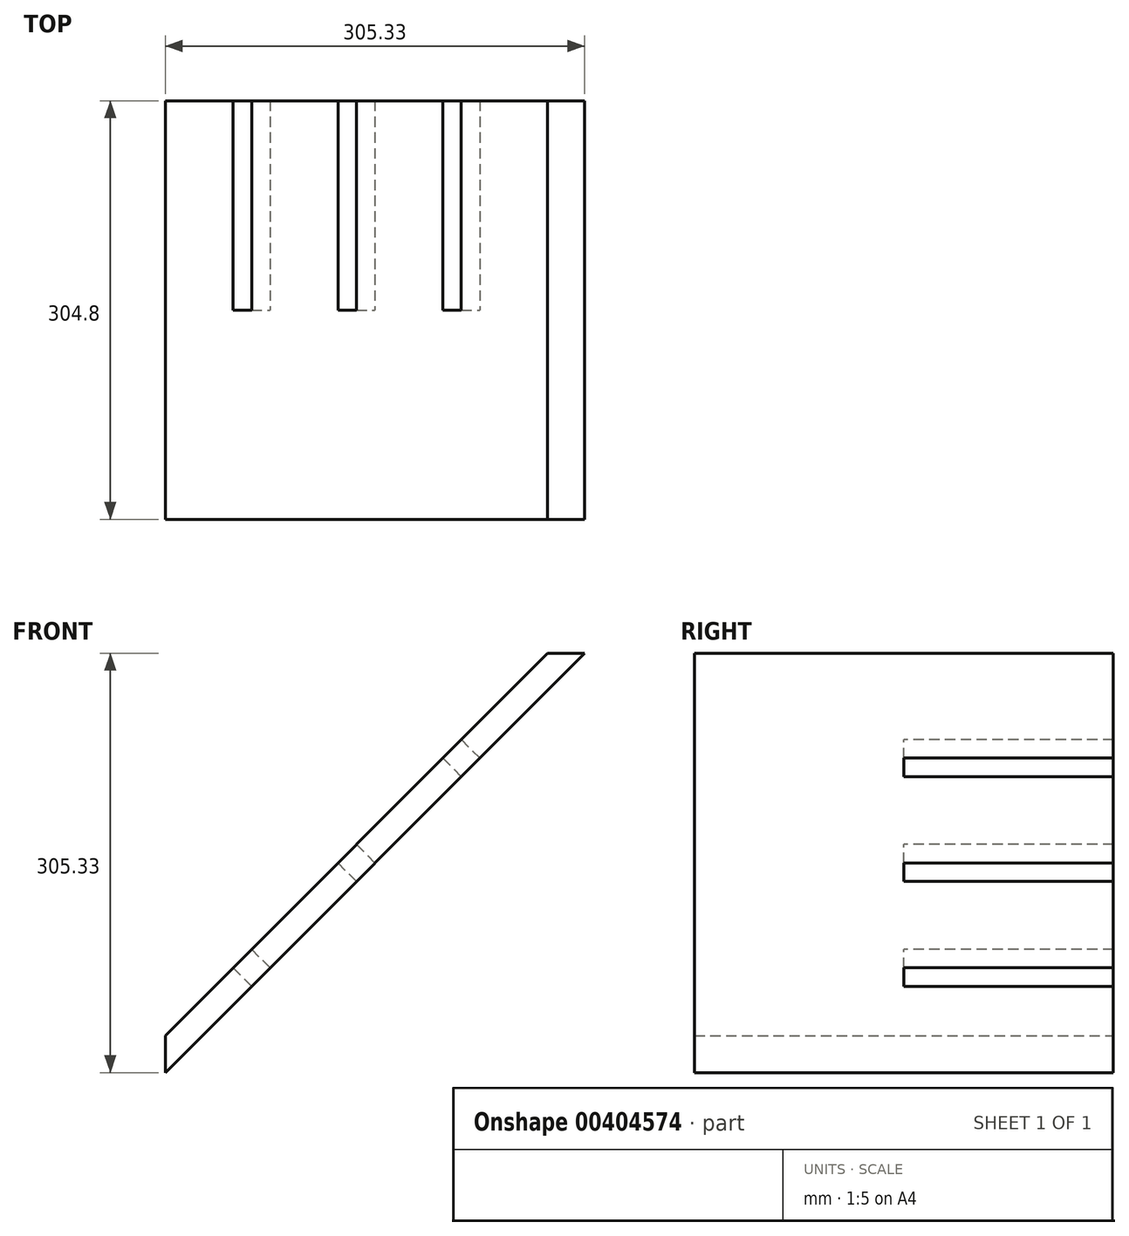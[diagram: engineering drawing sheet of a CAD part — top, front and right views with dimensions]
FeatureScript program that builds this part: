
annotation { "Feature Type Name" : "Feature", "Feature Type Description" : "" }
export const myFeature = defineFeature(function(context is Context, id is Id, definition is map)
    precondition{}
    {
        {
            var Q0;
            Q0=qCreatedBy(makeId("Front.planeOp"),FACE);
            var sketch = newSketch(context, id + "F0", { "sketchPlane" : qUnion([Q0])});
            skLineSegment(sketch, "E0.left", {"start": v(-421.52, 0) * mm, "end": v(-421.52, 26.94) * mm});
            skPoint(sketch, "E0.middle", {"position": v(22.97, 488.94) * mm});
            skLineSegment(sketch, "E1", {"start": v(-421.52, 0) * mm, "end": v(-116.2, 305.33) * mm});
            skLineSegment(sketch, "E2", {"start": v(-421.52, 26.94) * mm, "end": v(-143.14, 305.33) * mm});
            skLineSegment(sketch, "E3", {"start": v(-116.2, 305.33) * mm, "end": v(-143.14, 305.33) * mm});
            skSolve(sketch);
        }
        {
            var Q0;
            Q0=qSketchRegion(id+"F0",true);
            extrude(context, id + "F1", {"entities" : qUnion([Q0]), "endBound" : BoundingType.SYMMETRIC, "depth" : 304.8 * mm});
        }
        {
            var Q0;
            Q0=makeQuery(id+"F1.opExtrude","SWEPT_FACE",FACE,{"disambiguationData":[OSD([sQuery(id+"F0.wireOp",EDGE,"E2")])]});
            var sketch = newSketch(context, id + "F2", { "sketchPlane" : qUnion([Q0])});
            skLineSegment(sketch, "E4.bottom", {"start": v(-152.4, -209.16) * mm, "end": v(0, -209.16) * mm});
            skLineSegment(sketch, "E4.top", {"start": v(-152.4, -190.11) * mm, "end": v(0, -190.11) * mm});
            skLineSegment(sketch, "E4.left", {"start": v(-152.4, -209.16) * mm, "end": v(-152.4, -190.11) * mm});
            skLineSegment(sketch, "E4.right", {"start": v(0, -209.16) * mm, "end": v(0, -190.11) * mm});
            skLineSegment(sketch, "E5.bottom", {"start": v(-152.4, -101.21) * mm, "end": v(0, -101.21) * mm});
            skLineSegment(sketch, "E5.top", {"start": v(-152.4, -82.16) * mm, "end": v(0, -82.16) * mm});
            skLineSegment(sketch, "E5.left", {"start": v(-152.4, -101.21) * mm, "end": v(-152.4, -82.16) * mm});
            skLineSegment(sketch, "E5.right", {"start": v(0, -101.21) * mm, "end": v(0, -82.16) * mm});
            skLineSegment(sketch, "E6.bottom", {"start": v(-152.4, 6.74) * mm, "end": v(0, 6.74) * mm});
            skLineSegment(sketch, "E6.top", {"start": v(-152.4, 25.79) * mm, "end": v(0, 25.79) * mm});
            skLineSegment(sketch, "E6.left", {"start": v(-152.4, 6.74) * mm, "end": v(-152.4, 25.79) * mm});
            skLineSegment(sketch, "E6.right", {"start": v(0, 6.74) * mm, "end": v(0, 25.79) * mm});
            skSolve(sketch);
        }
        {
            var Q0;
            Q0=qSketchRegion(id+"F2",true);
            extrude(context, id + "F3", {"entities" : qUnion([Q0]), "operationType" : NewBodyOperationType.REMOVE, "oppositeDirection" : true, "depth" : 19.05 * mm});
        }
    });
